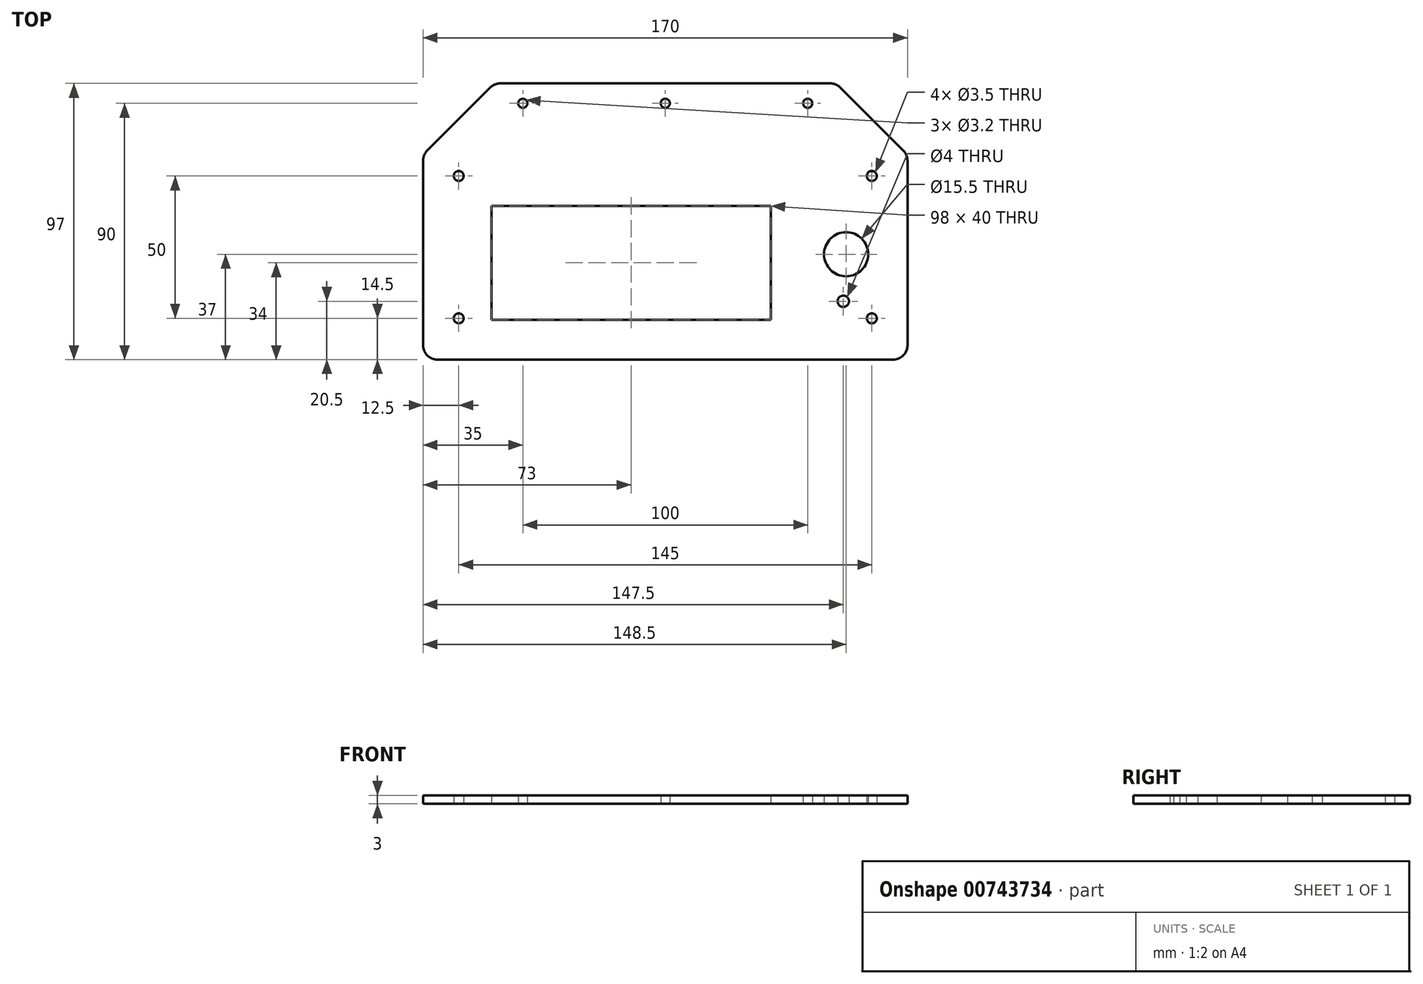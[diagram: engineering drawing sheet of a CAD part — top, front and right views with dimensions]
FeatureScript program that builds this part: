
annotation { "Feature Type Name" : "Feature", "Feature Type Description" : "" }
export const myFeature = defineFeature(function(context is Context, id is Id, definition is map)
    precondition{}
    {
        {
            var Q0;
            Q0=qCreatedBy(makeId("Top.planeOp"),FACE);
            var sketch = newSketch(context, id + "F0", { "sketchPlane" : qUnion([Q0])});
            skLineSegment(sketch, "E0.bottom", {"start": v(-75, 12) * mm, "end": v(75, 12) * mm});
            skLineSegment(sketch, "E0.top", {"start": v(-75, 67) * mm, "end": v(75, 67) * mm});
            skLineSegment(sketch, "E0.left", {"start": v(-75, 12) * mm, "end": v(-75, 67) * mm});
            skLineSegment(sketch, "E0.right", {"start": v(75, 12) * mm, "end": v(75, 67) * mm});
            skCircle(sketch, "E1", {"center": v(-72.5, 64.5) * mm, "radius": 1.75 * mm});
            skLineSegment(sketch, "E2.bottom", {"start": v(-61, 54) * mm, "end": v(37, 54) * mm});
            skLineSegment(sketch, "E2.top", {"start": v(-61, 14) * mm, "end": v(37, 14) * mm});
            skLineSegment(sketch, "E2.left", {"start": v(-61, 54) * mm, "end": v(-61, 14) * mm});
            skLineSegment(sketch, "E2.right", {"start": v(37, 54) * mm, "end": v(37, 14) * mm});
            skCircle(sketch, "E3", {"center": v(63.5, 37) * mm, "radius": 7.75 * mm});
            skCircle(sketch, "E4", {"center": v(62.5, 20.5) * mm, "radius": 2 * mm});
            skLineSegment(sketch, "E5.bottom", {"start": v(-85, 0) * mm, "end": v(85, 0) * mm});
            skLineSegment(sketch, "E5.top", {"start": v(-85, 97) * mm, "end": v(85, 97) * mm});
            skLineSegment(sketch, "E5.left", {"start": v(-85, 0) * mm, "end": v(-85, 97) * mm});
            skLineSegment(sketch, "E5.right", {"start": v(85, 0) * mm, "end": v(85, 97) * mm});
            skLineSegment(sketch, "E6", {"start": v(-85, 72) * mm, "end": v(-60, 97) * mm});
            skCircle(sketch, "E7.0.1.0", {"center": v(-72.5, 14.5) * mm, "radius": 1.75 * mm});
            skCircle(sketch, "E7.1.0.0", {"center": v(72.5, 64.5) * mm, "radius": 1.75 * mm});
            skCircle(sketch, "E7.1.1.0", {"center": v(72.5, 14.5) * mm, "radius": 1.75 * mm});
            skCircle(sketch, "E7.2.0.0", {"center": v(217.5, 64.5) * mm, "radius": 1.75 * mm});
            skCircle(sketch, "E7.2.1.0", {"center": v(217.5, 14.5) * mm, "radius": 1.75 * mm});
            skLineSegment(sketch, "E7.direction1", {"start": v(-72.5, 64.5) * mm, "end": v(72.5, 64.5) * mm, "construction": true});
            skLineSegment(sketch, "E7.direction2", {"start": v(-72.5, 64.5) * mm, "end": v(-72.5, 14.5) * mm, "construction": true});
            skLineSegment(sketch, "E8.MirrorCS", {"start": v(85, 72) * mm, "end": v(60, 97) * mm});
            skCircle(sketch, "E9", {"center": v(-50, 90) * mm, "radius": 1.6 * mm});
            skCircle(sketch, "E10.1.0.0", {"center": v(0, 90) * mm, "radius": 1.6 * mm});
            skCircle(sketch, "E10.2.0.0", {"center": v(50, 90) * mm, "radius": 1.6 * mm});
            skLineSegment(sketch, "E10.direction1", {"start": v(-50, 90) * mm, "end": v(0, 90) * mm, "construction": true});
            skSolve(sketch);
        }
        {
            var Q0;
            {var subQ10=sQuery(id+"F0.wireOp",EDGE,"E0.bottom");Q0=makeQuery(id+"F0.imprint","IMPRINT",FACE,{"disambiguationData":[TD([[makeQuery(id+"F0.imprint","IMPRINT",EDGE,{"derivedFrom":subQ10}),-1.0]])]});}
            var Q1;
            {var subQ4=sQuery(id+"F0.wireOp",EDGE,"E0.bottom");Q1=makeQuery(id+"F0.imprint","IMPRINT",FACE,{"disambiguationData":[TD([[makeQuery(id+"F0.imprint","IMPRINT",EDGE,{"derivedFrom":subQ4}),1.0]])]});}
            extrude(context, id + "F1", {"entities" : qUnion([Q0, Q1]), "depth" : 3 * mm, "offsetDistance" : 25 * mm});
        }
        {
            var Q0;
            Q0=makeQuery(id+"F1.opExtrude","SWEPT_EDGE",EDGE,{"disambiguationData":[OSD([sQuery(id+"F0.wireOp",EDGE,"E5.bottom"),sQuery(id+"F0.wireOp",EDGE,"E5.right")])]});
            var Q1;
            Q1=makeQuery(id+"F1.opExtrude","SWEPT_EDGE",EDGE,{"disambiguationData":[OSD([sQuery(id+"F0.wireOp",EDGE,"E5.right"),sQuery(id+"F0.wireOp",EDGE,"E8.MirrorCS")])]});
            var Q2;
            Q2=makeQuery(id+"F1.opExtrude","SWEPT_EDGE",EDGE,{"disambiguationData":[OSD([sQuery(id+"F0.wireOp",EDGE,"E5.bottom"),sQuery(id+"F0.wireOp",EDGE,"E5.left")])]});
            var Q3;
            Q3=makeQuery(id+"F1.opExtrude","SWEPT_EDGE",EDGE,{"disambiguationData":[OSD([sQuery(id+"F0.wireOp",EDGE,"E5.left"),sQuery(id+"F0.wireOp",EDGE,"E6")])]});
            var Q4;
            Q4=makeQuery(id+"F1.opExtrude","SWEPT_EDGE",EDGE,{"disambiguationData":[OSD([sQuery(id+"F0.wireOp",EDGE,"E5.top"),sQuery(id+"F0.wireOp",EDGE,"E6")])]});
            var Q5;
            Q5=makeQuery(id+"F1.opExtrude","SWEPT_EDGE",EDGE,{"disambiguationData":[OSD([sQuery(id+"F0.wireOp",EDGE,"E5.top"),sQuery(id+"F0.wireOp",EDGE,"E8.MirrorCS")])]});
            fillet(context, id + "F2", {"entities" : qUnion([Q0, Q1, Q2, Q3, Q4, Q5]), "radius" : 5 * mm, "tangentPropagation" : true, "allowEdgeOverflow" : false});
        }
    });
